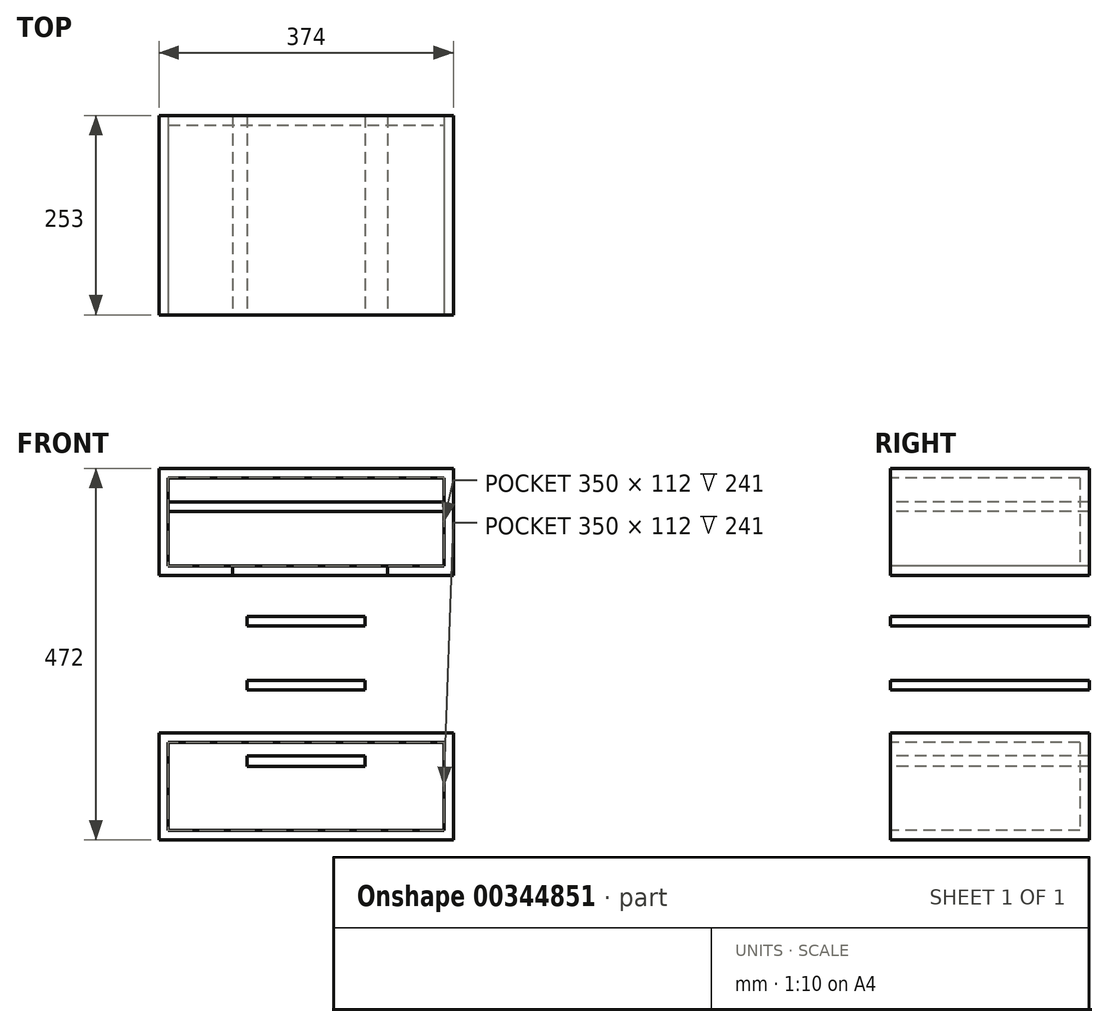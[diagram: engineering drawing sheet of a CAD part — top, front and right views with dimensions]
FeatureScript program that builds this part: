
annotation { "Feature Type Name" : "Feature", "Feature Type Description" : "" }
export const myFeature = defineFeature(function(context is Context, id is Id, definition is map)
    precondition{}
    {
        {
            var Q0;
            Q0=qCreatedBy(makeId("Front.planeOp"),FACE);
            var sketch = newSketch(context, id + "F0", { "sketchPlane" : qUnion([Q0])});
            skLineSegment(sketch, "E0.bottom", {"start": v(-187, 236) * mm, "end": v(187, 236) * mm});
            skLineSegment(sketch, "E0.top", {"start": v(-187, -236) * mm, "end": v(187, -236) * mm});
            skLineSegment(sketch, "E0.left", {"start": v(-187, 236) * mm, "end": v(-187, -236) * mm});
            skLineSegment(sketch, "E0.right", {"start": v(187, 236) * mm, "end": v(187, -236) * mm});
            skPoint(sketch, "E0.middle", {"position": v(0, 0) * mm});
            skLineSegment(sketch, "E1.bottom", {"start": v(-187, 100) * mm, "end": v(187, 100) * mm});
            skLineSegment(sketch, "E1.top", {"start": v(-187, -100) * mm, "end": v(187, -100) * mm});
            skLineSegment(sketch, "E1.left", {"start": v(-187, 100) * mm, "end": v(-187, -100) * mm});
            skLineSegment(sketch, "E1.right", {"start": v(187, 100) * mm, "end": v(187, -100) * mm});
            skLineSegment(sketch, "E2.bottom", {"start": v(-87, 100) * mm, "end": v(87, 100) * mm});
            skLineSegment(sketch, "E2.top", {"start": v(-87, -100) * mm, "end": v(87, -100) * mm});
            skLineSegment(sketch, "E2.left", {"start": v(-87, 100) * mm, "end": v(-87, -100) * mm});
            skLineSegment(sketch, "E2.right", {"start": v(87, 100) * mm, "end": v(87, -100) * mm});
            skSolve(sketch);
        }
        {
            var Q0;
            {var subQ1=sQuery(id+"F0.wireOp",EDGE,"E0.top");Q0=makeQuery(id+"F0.imprint","IMPRINT",FACE,{"disambiguationData":[TD([[makeQuery(id+"F0.imprint","IMPRINT",EDGE,{"derivedFrom":subQ1}),1.0]])]});}
            var Q1;
            Q1=makeQuery(id+"F0.imprint","IMPRINT",FACE,{"disambiguationData":[TD([[makeQuery(id+"F0.imprint","IMPRINT",EDGE,{"derivedFrom":sQuery(id+"F0.wireOp",EDGE,"E2.bottom")}),-1.0]])]});
            var Q2;
            {var subQ5=sQuery(id+"F0.wireOp",EDGE,"E0.bottom");Q2=makeQuery(id+"F0.imprint","IMPRINT",FACE,{"disambiguationData":[TD([[makeQuery(id+"F0.imprint","IMPRINT",EDGE,{"derivedFrom":subQ5}),-1.0]])]});}
            extrude(context, id + "F1", {"entities" : qUnion([Q0, Q1, Q2]), "oppositeDirection" : true, "depth" : 253 * mm});
        }
        {
            var Q0;
            Q0=makeQuery(id+"F1.opExtrude","CAP_FACE",FACE,{"disambiguationData":[OSD([sQuery(id+"F0.wireOp",EDGE,"E0.bottom"),sQuery(id+"F0.wireOp",EDGE,"E0.top"),sQuery(id+"F0.wireOp",EDGE,"E0.left"),sQuery(id+"F0.wireOp",EDGE,"E0.right"),sQuery(id+"F0.wireOp",EDGE,"E1.bottom"),sQuery(id+"F0.wireOp",EDGE,"E1.top"),sQuery(id+"F0.wireOp",EDGE,"E2.left"),sQuery(id+"F0.wireOp",EDGE,"E2.right")])],"isStart":true});
            shell(context, id + "F2", {"entities" : qUnion([Q0]), "thickness" : 12 * mm});
        }
        {
            var Q0;
            Q0=makeQuery(id+"F1.opExtrude","CAP_FACE",FACE,{"disambiguationData":[OSD([sQuery(id+"F0.wireOp",EDGE,"E0.bottom"),sQuery(id+"F0.wireOp",EDGE,"E0.top"),sQuery(id+"F0.wireOp",EDGE,"E0.left"),sQuery(id+"F0.wireOp",EDGE,"E0.right"),sQuery(id+"F0.wireOp",EDGE,"E1.bottom"),sQuery(id+"F0.wireOp",EDGE,"E1.top"),sQuery(id+"F0.wireOp",EDGE,"E2.left"),sQuery(id+"F0.wireOp",EDGE,"E2.right")])],"isStart":true});
            var sketch = newSketch(context, id + "F3", { "sketchPlane" : qUnion([Q0])});
            skLineSegment(sketch, "E3.bottom", {"start": v(-93.08, 112) * mm, "end": v(103.77, 112) * mm});
            skLineSegment(sketch, "E3.top", {"start": v(-93.08, 100) * mm, "end": v(103.77, 100) * mm});
            skLineSegment(sketch, "E3.left", {"start": v(-93.08, 112) * mm, "end": v(-93.08, 100) * mm});
            skLineSegment(sketch, "E3.right", {"start": v(103.77, 112) * mm, "end": v(103.77, 100) * mm});
            skLineSegment(sketch, "E4.bottom", {"start": v(-75, -81.76) * mm, "end": v(-87, -81.76) * mm});
            skLineSegment(sketch, "E4.top", {"start": v(-75, -229.56) * mm, "end": v(-87, -229.56) * mm});
            skLineSegment(sketch, "E4.left", {"start": v(-75, -81.76) * mm, "end": v(-75, -229.56) * mm});
            skLineSegment(sketch, "E4.right", {"start": v(-87, -81.76) * mm, "end": v(-87, -229.56) * mm});
            skPoint(sketch, "E5.oppositeSnap0", {"position": v(-81, -229.56) * mm});
            skLineSegment(sketch, "E5.bottom", {"start": v(75, -87.42) * mm, "end": v(87, -87.42) * mm});
            skLineSegment(sketch, "E5.top", {"start": v(75, -229.56) * mm, "end": v(87, -229.56) * mm});
            skLineSegment(sketch, "E5.left", {"start": v(75, -87.42) * mm, "end": v(75, -229.56) * mm});
            skLineSegment(sketch, "E5.right", {"start": v(87, -87.42) * mm, "end": v(87, -229.56) * mm});
            skLineSegment(sketch, "E6.bottom", {"start": v(-180.5, 193.13) * mm, "end": v(175, 193.13) * mm});
            skLineSegment(sketch, "E6.top", {"start": v(-180.5, 181.13) * mm, "end": v(175, 181.13) * mm});
            skLineSegment(sketch, "E6.left", {"start": v(-180.5, 193.13) * mm, "end": v(-180.5, 181.13) * mm});
            skLineSegment(sketch, "E6.right", {"start": v(175, 193.13) * mm, "end": v(175, 181.13) * mm});
            skLineSegment(sketch, "E7.bottom", {"start": v(-75, -129.56) * mm, "end": v(75, -129.56) * mm});
            skLineSegment(sketch, "E7.top", {"start": v(-75, -142.77) * mm, "end": v(75, -142.77) * mm});
            skLineSegment(sketch, "E7.left", {"start": v(-75, -129.56) * mm, "end": v(-75, -142.77) * mm});
            skLineSegment(sketch, "E7.right", {"start": v(75, -129.56) * mm, "end": v(75, -142.77) * mm});
            skLineSegment(sketch, "E8.left", {"start": v(-75, 0) * mm, "end": v(-75, -12.58) * mm});
            skLineSegment(sketch, "E8.right", {"start": v(75, 0) * mm, "end": v(75, -12.58) * mm});
            skLineSegment(sketch, "E9.bottom", {"start": v(-75, 35.85) * mm, "end": v(75, 35.85) * mm});
            skLineSegment(sketch, "E9.top", {"start": v(-75, 47.85) * mm, "end": v(75, 47.85) * mm});
            skLineSegment(sketch, "E9.left", {"start": v(-75, 35.85) * mm, "end": v(-75, 47.85) * mm});
            skLineSegment(sketch, "E9.right", {"start": v(75, 35.85) * mm, "end": v(75, 47.85) * mm});
            skLineSegment(sketch, "E10.bottom", {"start": v(-75, -33.28) * mm, "end": v(75, -33.28) * mm});
            skLineSegment(sketch, "E10.top", {"start": v(-75, -45.28) * mm, "end": v(75, -45.28) * mm});
            skLineSegment(sketch, "E10.left", {"start": v(-75, -33.28) * mm, "end": v(-75, -45.28) * mm});
            skLineSegment(sketch, "E10.right", {"start": v(75, -33.28) * mm, "end": v(75, -45.28) * mm});
            skSolve(sketch);
        }
        {
            var Q0;
            {var subQ0=sQuery(id+"F3.wireOp",EDGE,"E6.right");Q0=makeQuery(id+"F3.imprint","IMPRINT",FACE,{"disambiguationData":[TD([[makeQuery(id+"F3.imprint","IMPRINT",EDGE,{"derivedFrom":subQ0}),-1.0]])]});}
            var Q1;
            {var subQ0=sQuery(id+"F3.wireOp",EDGE,"E3.bottom");var subQ1=sQuery(id+"F0.wireOp",EDGE,"E2.left");var subQ2=makeQuery(id+"F2.opShell","OFFSET_EDGE",EDGE,{"disambiguationData":[OSD([subQ1]),TDD([makeQuery(id+"F1.opExtrude","CAP_EDGE",EDGE,{"disambiguationData":[OSD([subQ1])],"isStart":true})])]});var subQ3=makeQuery(id+"F3.imprint","INTERSECT",VERTEX,{"derivedFrom":[subQ2,subQ0]});Q1=makeQuery(id+"F3.imprint","IMPRINT",FACE,{"disambiguationData":[TD([[makeQuery(id+"F3.imprint","IMPRINT",EDGE,{"disambiguationData":[TD([[subQ3,-1.0]])],"derivedFrom":subQ0}),-1.0]])]});}
            var Q2;
            Q2=makeQuery(id+"F3.imprint","IMPRINT",FACE,{"disambiguationData":[TD([[makeQuery(id+"F3.imprint","IMPRINT",EDGE,{"derivedFrom":sQuery(id+"F3.wireOp",EDGE,"E9.bottom")}),1.0]])]});
            var Q3;
            Q3=makeQuery(id+"F3.imprint","IMPRINT",FACE,{"disambiguationData":[TD([[makeQuery(id+"F3.imprint","IMPRINT",EDGE,{"derivedFrom":sQuery(id+"F3.wireOp",EDGE,"E10.bottom")}),-1.0]])]});
            var Q4;
            Q4=makeQuery(id+"F3.imprint","IMPRINT",FACE,{"disambiguationData":[TD([[makeQuery(id+"F3.imprint","IMPRINT",EDGE,{"derivedFrom":sQuery(id+"F3.wireOp",EDGE,"E7.bottom")}),-1.0]])]});
            var Q5;
            {var subQ0=sQuery(id+"F3.wireOp",EDGE,"E7.left");Q5=makeQuery(id+"F3.imprint","IMPRINT",FACE,{"disambiguationData":[TD([[makeQuery(id+"F3.imprint","IMPRINT",EDGE,{"derivedFrom":subQ0}),-1.0]])]});}
            var Q6;
            {var subQ0=sQuery(id+"F3.wireOp",EDGE,"E7.right");Q6=makeQuery(id+"F3.imprint","IMPRINT",FACE,{"disambiguationData":[TD([[makeQuery(id+"F3.imprint","IMPRINT",EDGE,{"derivedFrom":subQ0}),1.0]])]});}
            extrude(context, id + "F4", {"entities" : qUnion([Q0, Q1, Q2, Q3, Q4, Q5, Q6]), "oppositeDirection" : true, "depth" : 253 * mm});
        }
    });
